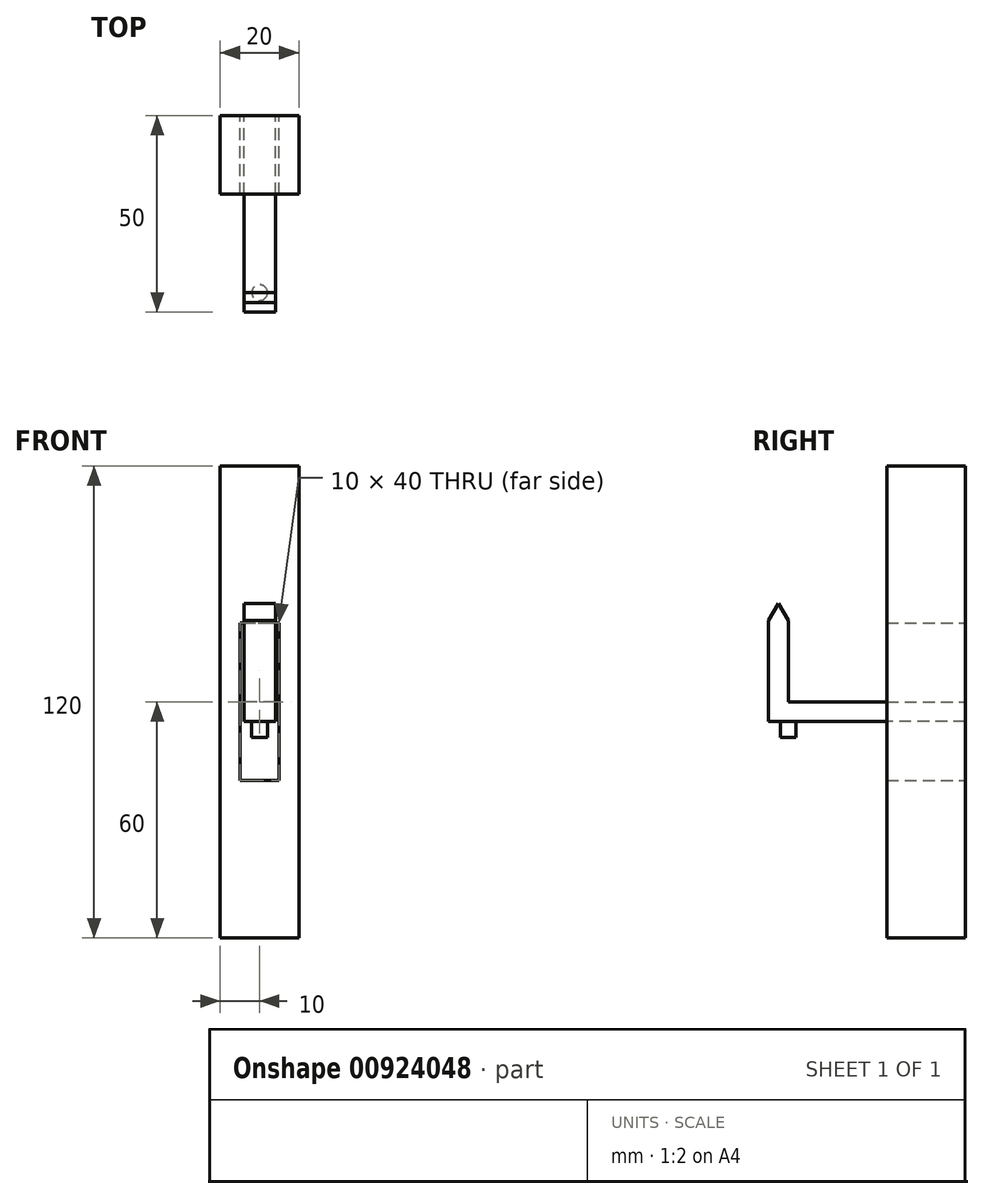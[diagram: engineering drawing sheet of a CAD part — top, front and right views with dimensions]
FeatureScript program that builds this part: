
annotation { "Feature Type Name" : "Feature", "Feature Type Description" : "" }
export const myFeature = defineFeature(function(context is Context, id is Id, definition is map)
    precondition{}
    {
        {
            var Q0;
            Q0=qCreatedBy(makeId("Front.planeOp"),FACE);
            var sketch = newSketch(context, id + "F0", { "sketchPlane" : qUnion([Q0])});
            skLineSegment(sketch, "E0.bottom", {"start": v(-10, 60) * mm, "end": v(10, 60) * mm});
            skLineSegment(sketch, "E0.top", {"start": v(-10, -60) * mm, "end": v(10, -60) * mm});
            skLineSegment(sketch, "E0.left", {"start": v(-10, 60) * mm, "end": v(-10, -60) * mm});
            skLineSegment(sketch, "E0.right", {"start": v(10, 60) * mm, "end": v(10, -60) * mm});
            skLineSegment(sketch, "E1.bottom", {"start": v(-5, 20) * mm, "end": v(5, 20) * mm});
            skLineSegment(sketch, "E1.top", {"start": v(-5, -20) * mm, "end": v(5, -20) * mm});
            skLineSegment(sketch, "E1.left", {"start": v(-5, 20) * mm, "end": v(-5, -20) * mm});
            skLineSegment(sketch, "E1.right", {"start": v(5, 20) * mm, "end": v(5, -20) * mm});
            skSolve(sketch);
        }
        {
            var Q0;
            Q0=makeQuery(id+"F0.imprint","IMPRINT",FACE,{"disambiguationData":[TD([[makeQuery(id+"F0.imprint","IMPRINT",EDGE,{"derivedFrom":sQuery(id+"F0.wireOp",EDGE,"E0.bottom")}),-1.0]])]});
            extrude(context, id + "F1", {"entities" : qUnion([Q0]), "depth" : 20 * mm, "offsetDistance" : 25 * mm});
        }
        {
            var Q0;
            Q0=qCreatedBy(makeId("Right.planeOp"),FACE);
            var sketch = newSketch(context, id + "F2", { "sketchPlane" : qUnion([Q0])});
            skLineSegment(sketch, "E2", {"start": v(0, -5) * mm, "end": v(-50, -5) * mm});
            skLineSegment(sketch, "E3", {"start": v(-50, -5) * mm, "end": v(-50, 20.67) * mm});
            skLineSegment(sketch, "E4", {"start": v(-50, 20.67) * mm, "end": v(-47.5, 25) * mm});
            skLineSegment(sketch, "E5", {"start": v(-47.5, 25) * mm, "end": v(-45, 20.67) * mm});
            skLineSegment(sketch, "E6", {"start": v(-45, 20.67) * mm, "end": v(-45, 0) * mm});
            skLineSegment(sketch, "E7", {"start": v(-45, 0) * mm, "end": v(0, 0) * mm});
            skLineSegment(sketch, "E8", {"start": v(0, 0) * mm, "end": v(0, -5) * mm});
            skSolve(sketch);
        }
        {
            var Q0;
            Q0=makeQuery(id+"F2.imprint","IMPRINT",FACE,{"disambiguationData":[TD([[makeQuery(id+"F2.imprint","IMPRINT",EDGE,{"derivedFrom":sQuery(id+"F2.wireOp",EDGE,"E2")}),-1.0]])]});
            extrude(context, id + "F3", {"entities" : qUnion([Q0]), "endBound" : BoundingType.SYMMETRIC, "depth" : 8 * mm, "offsetDistance" : 25 * mm});
        }
        {
            var Q0;
            Q0=makeQuery(id+"F3.opExtrude","SWEPT_FACE",FACE,{"disambiguationData":[OSD([sQuery(id+"F2.wireOp",EDGE,"E2")])]});
            var sketch = newSketch(context, id + "F4", { "sketchPlane" : qUnion([Q0])});
            skCircle(sketch, "E9", {"center": v(0, 45) * mm, "radius": 2 * mm});
            skSolve(sketch);
        }
        {
            var Q0;
            Q0=makeQuery(id+"F4.imprint","IMPRINT",FACE,{"disambiguationData":[TD([[makeQuery(id+"F4.imprint","IMPRINT",EDGE,{"derivedFrom":sQuery(id+"F4.wireOp",EDGE,"E9")}),1.0]])]});
            extrude(context, id + "F5", {"entities" : qUnion([Q0]), "operationType" : NewBodyOperationType.ADD, "depth" : 4 * mm, "offsetDistance" : 25 * mm});
        }
    });
